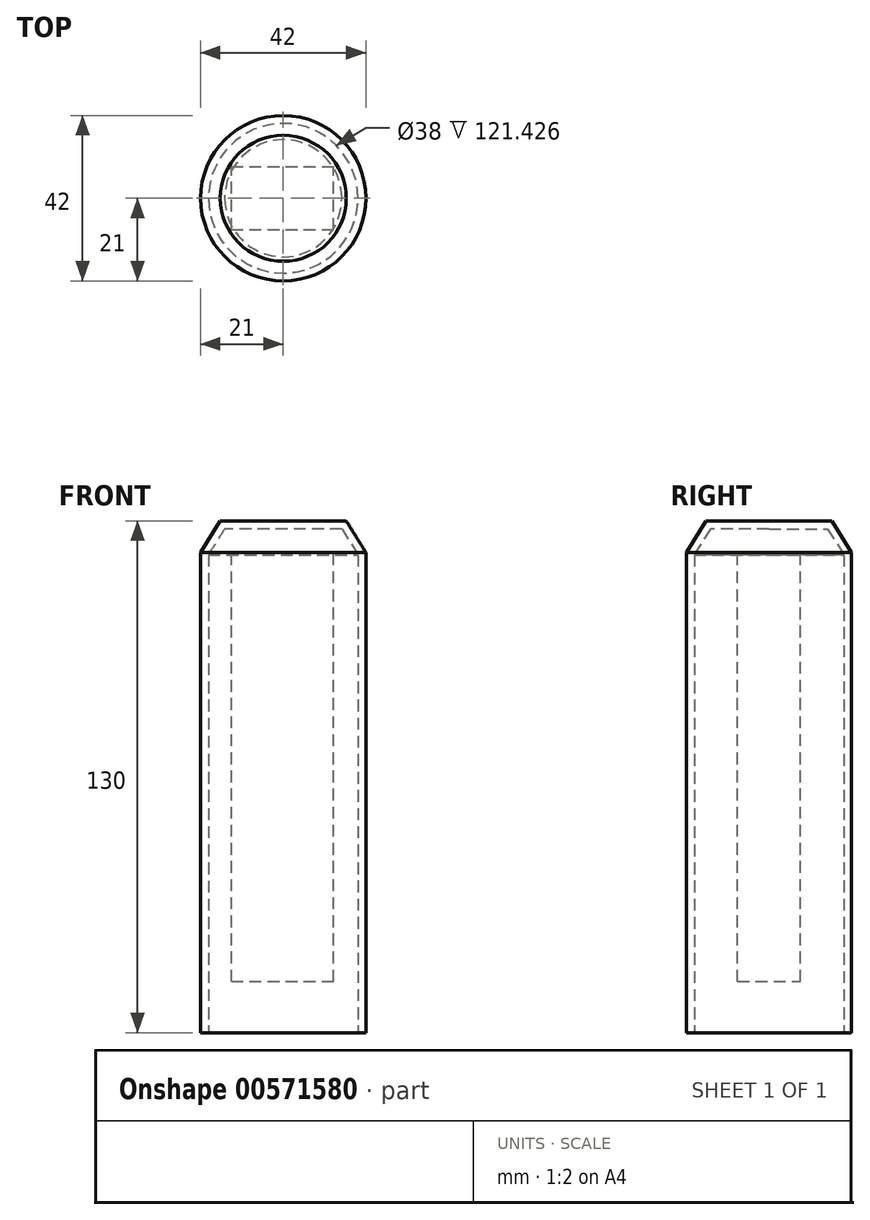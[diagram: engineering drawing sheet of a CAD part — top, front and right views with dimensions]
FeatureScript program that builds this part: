
annotation { "Feature Type Name" : "Feature", "Feature Type Description" : "" }
export const myFeature = defineFeature(function(context is Context, id is Id, definition is map)
    precondition{}
    {
        {
            var Q0;
            Q0=qCreatedBy(makeId("Top.planeOp"),FACE);
            var sketch = newSketch(context, id + "F0", { "sketchPlane" : qUnion([Q0])});
            skCircle(sketch, "E0", {"center": v(0, 0) * mm, "radius": 21 * mm});
            skSolve(sketch);
        }
        {
            var Q0;
            Q0=makeQuery(id+"F0.imprint","IMPRINT",FACE,{"disambiguationData":[TD([[makeQuery(id+"F0.imprint","IMPRINT",EDGE,{"derivedFrom":sQuery(id+"F0.wireOp",EDGE,"E0")}),1.0]])]});
            extrude(context, id + "F1", {"entities" : qUnion([Q0]), "depth" : 130 * mm, "offsetDistance" : 25 * mm});
        }
        {
            var Q0;
            Q0=makeQuery(id+"F1.opExtrude","CAP_EDGE",EDGE,{"disambiguationData":[OSD([sQuery(id+"F0.wireOp",EDGE,"E0")])],"isStart":false});
            chamfer(context, id + "F2", {"entities" : qUnion([Q0]), "chamferType" : ChamferType.TWO_OFFSETS, "width1" : 5 * mm, "oppositeDirection" : false, "width2" : 8 * mm, "tangentPropagation" : true});
        }
        {
            var Q0;
            Q0=makeQuery(id+"F1.opExtrude","CAP_FACE",FACE,{"disambiguationData":[OSD([sQuery(id+"F0.wireOp",EDGE,"E0")])],"isStart":true});
            shell(context, id + "F3", {"entities" : qUnion([Q0]), "thickness" : 2 * mm});
        }
        {
            var Q0;
            Q0=makeQuery(id+"F1.opExtrude","CAP_FACE",FACE,{"disambiguationData":[OSD([sQuery(id+"F0.wireOp",EDGE,"E0")])],"isStart":false});
            cPlane(context, id + "F4", {"entities" : qUnion([Q0]), "cplaneType" : CPlaneType.OFFSET, "offset" : 8 * mm, "oppositeDirection" : true, "width" : 150 * mm, "height" : 150 * mm});
        }
        {
            var Q0;
            Q0=qCreatedBy(id+"F4.planeOp",FACE);
            var sketch = newSketch(context, id + "F5", { "sketchPlane" : qUnion([Q0])});
            skLineSegment(sketch, "E1.bottom", {"start": v(-13.19, -8) * mm, "end": v(12.81, -8) * mm});
            skLineSegment(sketch, "E1.top", {"start": v(-13.19, 8) * mm, "end": v(12.81, 8) * mm});
            skLineSegment(sketch, "E1.left", {"start": v(-13.19, -8) * mm, "end": v(-13.19, 8) * mm});
            skLineSegment(sketch, "E1.right", {"start": v(12.81, -8) * mm, "end": v(12.81, 8) * mm});
            skSolve(sketch);
        }
        {
            var Q0;
            Q0=makeQuery(id+"F5.imprint","IMPRINT",FACE,{"disambiguationData":[TD([[makeQuery(id+"F5.imprint","IMPRINT",EDGE,{"derivedFrom":sQuery(id+"F5.wireOp",EDGE,"E1.bottom")}),1.0]])]});
            extrude(context, id + "F6", {"entities" : qUnion([Q0]), "oppositeDirection" : true, "depth" : 109 * mm, "offsetDistance" : 25 * mm});
        }
    });
